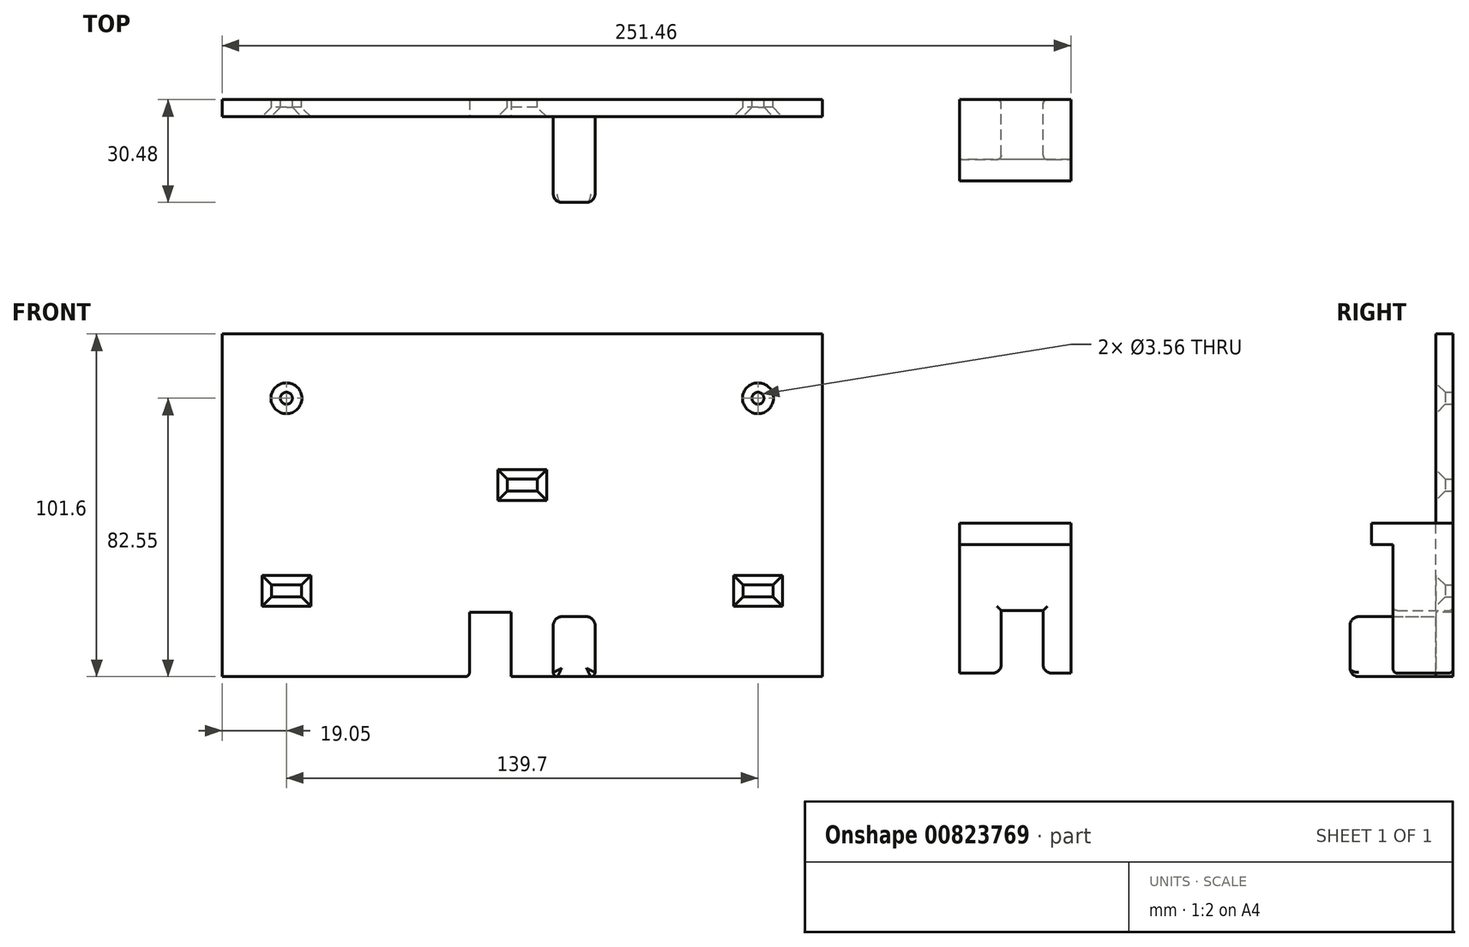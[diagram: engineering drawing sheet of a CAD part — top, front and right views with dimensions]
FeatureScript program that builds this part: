
annotation { "Feature Type Name" : "Feature", "Feature Type Description" : "" }
export const myFeature = defineFeature(function(context is Context, id is Id, definition is map)
    precondition{}
    {
        {
            var Q0;
            Q0=qCreatedBy(makeId("Front.planeOp"),FACE);
            var sketch = newSketch(context, id + "F0", { "sketchPlane" : qUnion([Q0])});
            skLineSegment(sketch, "E0.bottom", {"start": v(27.94, 8.9) * mm, "end": v(-27.94, 8.9) * mm});
            skLineSegment(sketch, "E0.top", {"start": v(27.94, -8.9) * mm, "end": v(-27.94, -8.9) * mm});
            skLineSegment(sketch, "E0.left", {"start": v(27.94, 8.9) * mm, "end": v(27.94, -8.9) * mm});
            skLineSegment(sketch, "E0.right", {"start": v(-27.94, 8.9) * mm, "end": v(-27.94, -8.9) * mm});
            skPoint(sketch, "E0.middle", {"position": v(0, 0) * mm});
            skSolve(sketch);
        }
        {
            var Q0;
            Q0=makeQuery(id+"F0.imprint","IMPRINT",FACE,{"disambiguationData":[TD([[makeQuery(id+"F0.imprint","IMPRINT",EDGE,{"derivedFrom":sQuery(id+"F0.wireOp",EDGE,"E0.bottom")}),1.0]])]});
            extrude(context, id + "F1", {"entities" : qUnion([Q0]), "depth" : 5.08 * mm, "offsetDistance" : 25.4 * mm});
        }
        {
            var Q0;
            Q0=makeQuery(id+"F1.opExtrude","CAP_FACE",FACE,{"disambiguationData":[OSD([sQuery(id+"F0.wireOp",EDGE,"E0.bottom"),sQuery(id+"F0.wireOp",EDGE,"E0.top"),sQuery(id+"F0.wireOp",EDGE,"E0.left"),sQuery(id+"F0.wireOp",EDGE,"E0.right")])],"isStart":false});
            var sketch = newSketch(context, id + "F2", { "sketchPlane" : qUnion([Q0])});
            skLineSegment(sketch, "E1.bottom", {"start": v(-15.6, 8.9) * mm, "end": v(-3.2, 8.9) * mm});
            skLineSegment(sketch, "E1.top", {"start": v(-15.6, -8.9) * mm, "end": v(-3.2, -8.9) * mm});
            skLineSegment(sketch, "E1.left", {"start": v(-15.6, 8.9) * mm, "end": v(-15.6, -8.9) * mm});
            skLineSegment(sketch, "E1.right", {"start": v(-3.2, 8.9) * mm, "end": v(-3.2, -8.9) * mm});
            skLineSegment(sketch, "E2.bottom", {"start": v(21.59, 8.9) * mm, "end": v(9.2, 8.9) * mm});
            skLineSegment(sketch, "E2.top", {"start": v(21.6, -8.9) * mm, "end": v(9.2, -8.9) * mm});
            skLineSegment(sketch, "E2.left", {"start": v(21.59, 8.9) * mm, "end": v(21.6, -8.9) * mm});
            skLineSegment(sketch, "E2.right", {"start": v(9.2, 8.9) * mm, "end": v(9.2, -8.9) * mm});
            skSolve(sketch);
        }
        {
            var Q0;
            Q0=makeQuery(id+"F2.imprint","IMPRINT",FACE,{"disambiguationData":[TD([[makeQuery(id+"F2.imprint","IMPRINT",EDGE,{"derivedFrom":sQuery(id+"F2.wireOp",EDGE,"E2.bottom")}),1.0]])]});
            extrude(context, id + "F3", {"entities" : qUnion([Q0]), "operationType" : NewBodyOperationType.ADD, "depth" : 25.4 * mm, "offsetDistance" : 25.4 * mm});
        }
        {
            var Q0;
            Q0=makeQuery(id+"F2.imprint","IMPRINT",FACE,{"disambiguationData":[TD([[makeQuery(id+"F2.imprint","IMPRINT",EDGE,{"derivedFrom":sQuery(id+"F2.wireOp",EDGE,"E1.bottom")}),1.0]])]});
            extrude(context, id + "F4", {"entities" : qUnion([Q0]), "operationType" : NewBodyOperationType.REMOVE, "endBound" : BoundingType.UP_TO_NEXT, "oppositeDirection" : true, "depth" : 25.4 * mm, "offsetDistance" : 25.4 * mm});
        }
        {
            var Q0;
            {var subQ2=sQuery(id+"F2.wireOp",EDGE,"E2.bottom");var subQ3=sQuery(id+"F0.wireOp",EDGE,"E0.left");var subQ6=sQuery(id+"F0.wireOp",EDGE,"E0.bottom");Q0=makeQuery(id+"F4.boolean.opBoolean","SPLIT",FACE,{"disambiguationData":[TD([makeQuery(id+"F1.opExtrude","SWEPT_FACE",FACE,{"disambiguationData":[OSD([subQ3])]})])],"derivedFrom":makeQuery(id+"F3.boolean.opBoolean","MERGE",FACE,{"derivedFrom":[makeQuery(id+"F1.opExtrude","SWEPT_FACE",FACE,{"disambiguationData":[OSD([subQ6])]}),makeQuery(id+"F3.opExtrude","SWEPT_FACE",FACE,{"disambiguationData":[OSD([subQ2])]})]})});}
            var sketch = newSketch(context, id + "F5", { "sketchPlane" : qUnion([Q0])});
            skLineSegment(sketch, "E3.bottom", {"start": v(27.94, 0) * mm, "end": v(-27.94, 0) * mm});
            skLineSegment(sketch, "E3.top", {"start": v(27.94, -5.08) * mm, "end": v(-27.94, -5.08) * mm});
            skLineSegment(sketch, "E3.left", {"start": v(27.94, 0) * mm, "end": v(27.94, -5.08) * mm});
            skLineSegment(sketch, "E3.right", {"start": v(-27.94, 0) * mm, "end": v(-27.94, -5.08) * mm});
            skSolve(sketch);
        }
        {
            var Q0;
            {var subQ6=sQuery(id+"F5.wireOp",EDGE,"E3.left");Q0=makeQuery(id+"F5.imprint","IMPRINT",FACE,{"disambiguationData":[TD([[makeQuery(id+"F5.imprint","IMPRINT",EDGE,{"derivedFrom":subQ6}),1.0]])]});}
            var Q1;
            {var subQ2=sQuery(id+"F5.wireOp",EDGE,"E3.right");Q1=makeQuery(id+"F5.imprint","IMPRINT",FACE,{"disambiguationData":[TD([[makeQuery(id+"F5.imprint","IMPRINT",EDGE,{"derivedFrom":subQ2}),1.0]])]});}
            extrude(context, id + "F6", {"entities" : qUnion([Q0, Q1]), "operationType" : NewBodyOperationType.ADD, "depth" : 6.35 * mm, "offsetDistance" : 25.4 * mm});
        }
        {
            var Q0;
            Q0=makeQuery(id+"F3.opExtrude","SWEPT_EDGE",EDGE,{"disambiguationData":[OSD([sQuery(id+"F0.wireOp",EDGE,"E0.bottom"),sQuery(id+"F2.wireOp",EDGE,"E2.bottom"),sQuery(id+"F2.wireOp",EDGE,"E2.left")])]});
            var Q1;
            Q1=makeQuery(id+"F3.opExtrude","CAP_EDGE",EDGE,{"disambiguationData":[OSD([sQuery(id+"F2.wireOp",EDGE,"E2.bottom")])],"isStart":false});
            var Q2;
            Q2=makeQuery(id+"F3.opExtrude","SWEPT_EDGE",EDGE,{"disambiguationData":[OSD([sQuery(id+"F0.wireOp",EDGE,"E0.bottom"),sQuery(id+"F2.wireOp",EDGE,"E2.bottom"),sQuery(id+"F2.wireOp",EDGE,"E2.right")])]});
            var Q3;
            Q3=makeQuery(id+"F3.opExtrude","CAP_EDGE",EDGE,{"disambiguationData":[OSD([sQuery(id+"F2.wireOp",EDGE,"E2.right")])],"isStart":false});
            var Q4;
            Q4=makeQuery(id+"F3.opExtrude","CAP_EDGE",EDGE,{"disambiguationData":[OSD([sQuery(id+"F2.wireOp",EDGE,"E2.left")])],"isStart":false});
            var Q5;
            Q5=makeQuery(id+"F3.opExtrude","CAP_EDGE",EDGE,{"disambiguationData":[OSD([sQuery(id+"F2.wireOp",EDGE,"E2.top")])],"isStart":false});
            fillet(context, id + "F7", {"entities" : qUnion([Q0, Q1, Q2, Q3, Q4, Q5]), "radius" : 2.54 * mm, "tangentPropagation" : true, "allowEdgeOverflow" : false});
        }
        {
            var Q0;
            Q0=qCreatedBy(makeId("Front.planeOp"),FACE);
            var sketch = newSketch(context, id + "F8", { "sketchPlane" : qUnion([Q0])});
            skLineSegment(sketch, "E4.bottom", {"start": v(129.54, 36.6) * mm, "end": v(162.56, 36.6) * mm});
            skLineSegment(sketch, "E4.top", {"start": v(129.54, -7.84) * mm, "end": v(162.56, -7.84) * mm});
            skLineSegment(sketch, "E4.left", {"start": v(129.54, 36.6) * mm, "end": v(129.54, -7.84) * mm});
            skLineSegment(sketch, "E4.right", {"start": v(162.56, 36.6) * mm, "end": v(162.56, -7.84) * mm});
            skLineSegment(sketch, "E5.bottom", {"start": v(154.33, -7.84) * mm, "end": v(141.94, -7.84) * mm});
            skLineSegment(sketch, "E5.top", {"start": v(154.33, 10.7) * mm, "end": v(141.94, 10.7) * mm});
            skLineSegment(sketch, "E5.left", {"start": v(154.33, -7.84) * mm, "end": v(154.33, 10.7) * mm});
            skLineSegment(sketch, "E5.right", {"start": v(141.94, -7.84) * mm, "end": v(141.94, 10.7) * mm});
            skSolve(sketch);
        }
        {
            var Q0;
            Q0=makeQuery(id+"F8.imprint","IMPRINT",FACE,{"disambiguationData":[TD([[makeQuery(id+"F8.imprint","IMPRINT",EDGE,{"derivedFrom":sQuery(id+"F8.wireOp",EDGE,"E4.bottom")}),-1.0]])]});
            extrude(context, id + "F9", {"entities" : qUnion([Q0]), "depth" : 17.78 * mm, "offsetDistance" : 25.4 * mm});
        }
        {
            var Q0;
            Q0=makeQuery(id+"F9.opExtrude","SWEPT_EDGE",EDGE,{"disambiguationData":[OSD([sQuery(id+"F8.wireOp",EDGE,"E4.top"),sQuery(id+"F8.wireOp",EDGE,"E5.bottom"),sQuery(id+"F8.wireOp",EDGE,"E5.right")])]});
            var Q1;
            Q1=makeQuery(id+"F9.opExtrude","SWEPT_EDGE",EDGE,{"disambiguationData":[OSD([sQuery(id+"F8.wireOp",EDGE,"E4.top"),sQuery(id+"F8.wireOp",EDGE,"E5.bottom"),sQuery(id+"F8.wireOp",EDGE,"E5.left")])]});
            fillet(context, id + "F10", {"entities" : qUnion([Q0, Q1]), "radius" : 2.54 * mm, "tangentPropagation" : true, "allowEdgeOverflow" : false});
        }
        {
            var Q0;
            Q0=makeQuery(id+"F9.opExtrude","CAP_FACE",FACE,{"disambiguationData":[OSD([sQuery(id+"F8.wireOp",EDGE,"E4.bottom"),sQuery(id+"F8.wireOp",EDGE,"E4.top"),sQuery(id+"F8.wireOp",EDGE,"E4.left"),sQuery(id+"F8.wireOp",EDGE,"E4.right"),sQuery(id+"F8.wireOp",EDGE,"E5.top"),sQuery(id+"F8.wireOp",EDGE,"E5.left"),sQuery(id+"F8.wireOp",EDGE,"E5.right")])],"isStart":false});
            var sketch = newSketch(context, id + "F11", { "sketchPlane" : qUnion([Q0])});
            skLineSegment(sketch, "E6.bottom", {"start": v(162.56, 36.6) * mm, "end": v(129.54, 36.6) * mm});
            skLineSegment(sketch, "E6.top", {"start": v(162.56, 30.26) * mm, "end": v(129.54, 30.26) * mm});
            skLineSegment(sketch, "E6.left", {"start": v(162.56, 36.6) * mm, "end": v(162.56, 30.26) * mm});
            skLineSegment(sketch, "E6.right", {"start": v(129.54, 36.6) * mm, "end": v(129.54, 30.26) * mm});
            skSolve(sketch);
        }
        {
            var Q0;
            Q0=makeQuery(id+"F11.imprint","IMPRINT",FACE,{"disambiguationData":[TD([[makeQuery(id+"F11.imprint","IMPRINT",EDGE,{"derivedFrom":sQuery(id+"F11.wireOp",EDGE,"E6.bottom")}),-1.0]])]});
            extrude(context, id + "F12", {"entities" : qUnion([Q0]), "operationType" : NewBodyOperationType.ADD, "depth" : 6.35 * mm, "offsetDistance" : 25.4 * mm});
        }
        {
            var Q0;
            Q0=makeQuery(id+"F4.boolean.opBoolean","COPY",EDGE,{"derivedFrom":makeQuery(id+"F4.opExtrude","SWEPT_EDGE",EDGE,{"disambiguationData":[OSD([sQuery(id+"F0.wireOp",EDGE,"E0.top"),sQuery(id+"F2.wireOp",EDGE,"E1.top"),sQuery(id+"F2.wireOp",EDGE,"E1.left")])]})});
            var Q1;
            Q1=makeQuery(id+"F4.boolean.opBoolean","COPY",EDGE,{"derivedFrom":makeQuery(id+"F4.opExtrude","SWEPT_EDGE",EDGE,{"disambiguationData":[OSD([sQuery(id+"F0.wireOp",EDGE,"E0.top"),sQuery(id+"F2.wireOp",EDGE,"E1.top"),sQuery(id+"F2.wireOp",EDGE,"E1.right")])]})});
            var Q2;
            Q2=makeQuery(id+"F3.opExtrude","SWEPT_EDGE",EDGE,{"disambiguationData":[OSD([sQuery(id+"F0.wireOp",EDGE,"E0.top"),sQuery(id+"F2.wireOp",EDGE,"E2.top"),sQuery(id+"F2.wireOp",EDGE,"E2.right")])]});
            var Q3;
            Q3=makeQuery(id+"F3.opExtrude","SWEPT_EDGE",EDGE,{"disambiguationData":[OSD([sQuery(id+"F0.wireOp",EDGE,"E0.top"),sQuery(id+"F2.wireOp",EDGE,"E2.top"),sQuery(id+"F2.wireOp",EDGE,"E2.left")])]});
            var Q4;
            Q4=makeQuery(id+"F9.opExtrude","CAP_EDGE",EDGE,{"disambiguationData":[OSD([sQuery(id+"F8.wireOp",EDGE,"E5.right")])],"isStart":true});
            var Q5;
            Q5=makeQuery(id+"F9.opExtrude","CAP_EDGE",EDGE,{"disambiguationData":[OSD([sQuery(id+"F8.wireOp",EDGE,"E5.top")])],"isStart":true});
            var Q6;
            Q6=makeQuery(id+"F9.opExtrude","CAP_EDGE",EDGE,{"disambiguationData":[OSD([sQuery(id+"F8.wireOp",EDGE,"E5.left")])],"isStart":true});
            var Q7;
            Q7=makeQuery(id+"F9.opExtrude","CAP_EDGE",EDGE,{"disambiguationData":[OSD([sQuery(id+"F8.wireOp",EDGE,"E5.left")])],"isStart":false});
            var Q8;
            Q8=makeQuery(id+"F9.opExtrude","CAP_EDGE",EDGE,{"disambiguationData":[OSD([sQuery(id+"F8.wireOp",EDGE,"E5.top")])],"isStart":false});
            var Q9;
            Q9=makeQuery(id+"F9.opExtrude","CAP_EDGE",EDGE,{"disambiguationData":[OSD([sQuery(id+"F8.wireOp",EDGE,"E5.right")])],"isStart":false});
            fillet(context, id + "F13", {"entities" : qUnion([Q0, Q1, Q2, Q3, Q4, Q5, Q6, Q7, Q8, Q9]), "radius" : 1.27 * mm, "tangentPropagation" : true, "allowEdgeOverflow" : false});
        }
        {
            var Q0;
            {var subQ2=sQuery(id+"F0.wireOp",EDGE,"E0.top");var subQ4=sQuery(id+"F0.wireOp",EDGE,"E0.bottom");var subQ6=makeQuery(id+"F3.opExtrude","SWEPT_FACE",FACE,{"disambiguationData":[OSD([sQuery(id+"F2.wireOp",EDGE,"E2.right")])]});var subQ7=sQuery(id+"F0.wireOp",EDGE,"E0.right");var subQ8=makeQuery(id+"F1.opExtrude","SWEPT_FACE",FACE,{"disambiguationData":[OSD([subQ7])]});var subQ9=sQuery(id+"F0.wireOp",EDGE,"E0.left");var subQ10=makeQuery(id+"F1.opExtrude","CAP_FACE",FACE,{"disambiguationData":[OSD([subQ4,subQ2,subQ9,subQ7])],"isStart":false});var subQ11=makeQuery(id+"F3.boolean.opBoolean","SPLIT",FACE,{"disambiguationData":[TD([subQ8])],"derivedFrom":subQ10});Q0=makeQuery(id+"F6.boolean.opBoolean","MERGE",FACE,{"derivedFrom":[makeQuery(id+"F3.boolean.opBoolean","SPLIT",FACE,{"disambiguationData":[TD([makeQuery(id+"F1.opExtrude","SWEPT_FACE",FACE,{"disambiguationData":[OSD([subQ9])]})])],"derivedFrom":subQ10}),makeQuery(id+"F4.boolean.opBoolean","SPLIT",FACE,{"disambiguationData":[TD([subQ8])],"derivedFrom":subQ11}),makeQuery(id+"F4.boolean.opBoolean","SPLIT",FACE,{"disambiguationData":[TD([subQ6])],"derivedFrom":subQ11}),makeQuery(id+"F6.opExtrude","SWEPT_FACE",FACE,{"disambiguationData":[OSD([sQuery(id+"F5.wireOp",EDGE,"E3.top")])]})]});}
            var sketch = newSketch(context, id + "F14", { "sketchPlane" : qUnion([Q0])});
            skLineSegment(sketch, "E7.bottom", {"start": v(-15.6, 8.9) * mm, "end": v(-3.2, 8.9) * mm});
            skLineSegment(sketch, "E7.top", {"start": v(-15.6, 10.16) * mm, "end": v(-3.2, 10.16) * mm});
            skLineSegment(sketch, "E7.left", {"start": v(-15.6, 8.9) * mm, "end": v(-15.6, 10.16) * mm});
            skLineSegment(sketch, "E7.right", {"start": v(-3.2, 8.9) * mm, "end": v(-3.2, 10.16) * mm});
            skSolve(sketch);
        }
        {
            var Q0;
            Q0=makeQuery(id+"F14.imprint","IMPRINT",FACE,{"disambiguationData":[TD([[makeQuery(id+"F14.imprint","IMPRINT",EDGE,{"derivedFrom":sQuery(id+"F14.wireOp",EDGE,"E7.bottom")}),-1.0]])]});
            extrude(context, id + "F15", {"entities" : qUnion([Q0]), "operationType" : NewBodyOperationType.REMOVE, "endBound" : BoundingType.UP_TO_NEXT, "oppositeDirection" : true, "depth" : 25.4 * mm, "offsetDistance" : 25.4 * mm});
        }
        {
            var Q0;
            {var subQ1=sQuery(id+"F0.wireOp",EDGE,"E0.top");var subQ3=sQuery(id+"F0.wireOp",EDGE,"E0.right");var subQ4=sQuery(id+"F0.wireOp",EDGE,"E0.bottom");var subQ7=sQuery(id+"F0.wireOp",EDGE,"E0.left");var subQ8=makeQuery(id+"F1.opExtrude","CAP_FACE",FACE,{"disambiguationData":[OSD([subQ4,subQ1,subQ7,subQ3])],"isStart":true});Q0=makeQuery(id+"F6.boolean.opBoolean","MERGE",FACE,{"derivedFrom":[makeQuery(id+"F4.boolean.opBoolean","SPLIT",FACE,{"disambiguationData":[TD([makeQuery(id+"F1.opExtrude","SWEPT_FACE",FACE,{"disambiguationData":[OSD([subQ7])]})])],"derivedFrom":subQ8}),makeQuery(id+"F4.boolean.opBoolean","SPLIT",FACE,{"disambiguationData":[TD([makeQuery(id+"F1.opExtrude","SWEPT_FACE",FACE,{"disambiguationData":[OSD([subQ3])]})])],"derivedFrom":subQ8}),makeQuery(id+"F6.opExtrude","SWEPT_FACE",FACE,{"disambiguationData":[OSD([sQuery(id+"F5.wireOp",EDGE,"E3.bottom")])]})]});}
            var sketch = newSketch(context, id + "F16", { "sketchPlane" : qUnion([Q0])});
            skLineSegment(sketch, "E8.bottom", {"start": v(-88.9, -8.9) * mm, "end": v(88.9, -8.9) * mm});
            skLineSegment(sketch, "E8.top", {"start": v(-88.9, 92.71) * mm, "end": v(88.9, 92.71) * mm});
            skLineSegment(sketch, "E8.left", {"start": v(-88.9, -8.9) * mm, "end": v(-88.9, 92.71) * mm});
            skLineSegment(sketch, "E8.right", {"start": v(88.9, -8.9) * mm, "end": v(88.9, 92.71) * mm});
            skPoint(sketch, "E9", {"position": v(0, 92.71) * mm});
            skCircle(sketch, "E10", {"center": v(0, 47.9) * mm, "radius": 1.78 * mm});
            skCircle(sketch, "E11", {"center": v(69.85, 73.66) * mm, "radius": 1.78 * mm});
            skCircle(sketch, "E12", {"center": v(69.85, 16.51) * mm, "radius": 1.78 * mm});
            skCircle(sketch, "E13", {"center": v(-69.85, 73.66) * mm, "radius": 1.78 * mm});
            skCircle(sketch, "E14", {"center": v(-69.85, 16.51) * mm, "radius": 1.78 * mm});
            skLineSegment(sketch, "E15.bottom", {"start": v(65.4, 18.29) * mm, "end": v(74.3, 18.29) * mm});
            skLineSegment(sketch, "E15.top", {"start": v(65.4, 14.73) * mm, "end": v(74.3, 14.73) * mm});
            skLineSegment(sketch, "E15.left", {"start": v(65.4, 18.29) * mm, "end": v(65.4, 14.73) * mm});
            skLineSegment(sketch, "E15.right", {"start": v(74.3, 18.29) * mm, "end": v(74.3, 14.73) * mm});
            skLineSegment(sketch, "E16.MirrorCS", {"start": v(-65.4, 14.73) * mm, "end": v(-74.3, 14.73) * mm});
            skLineSegment(sketch, "E17.MirrorCS", {"start": v(-65.4, 18.29) * mm, "end": v(-65.4, 14.73) * mm});
            skLineSegment(sketch, "E18.MirrorCS", {"start": v(-65.4, 18.29) * mm, "end": v(-74.3, 18.29) * mm});
            skLineSegment(sketch, "E19.MirrorCS", {"start": v(-74.3, 18.29) * mm, "end": v(-74.3, 14.73) * mm});
            skLineSegment(sketch, "E20.bottom", {"start": v(-4.45, 49.68) * mm, "end": v(4.45, 49.68) * mm});
            skLineSegment(sketch, "E20.top", {"start": v(-4.45, 46.13) * mm, "end": v(4.45, 46.13) * mm});
            skLineSegment(sketch, "E20.left", {"start": v(-4.45, 49.68) * mm, "end": v(-4.45, 46.13) * mm});
            skLineSegment(sketch, "E20.right", {"start": v(4.45, 49.68) * mm, "end": v(4.45, 46.13) * mm});
            skSolve(sketch);
        }
        {
            var Q0;
            Q0=makeQuery(id+"F16.imprint","IMPRINT",FACE,{"disambiguationData":[TD([[makeQuery(id+"F16.imprint","IMPRINT",EDGE,{"derivedFrom":sQuery(id+"F16.wireOp",EDGE,"E8.top")}),-1.0]])]});
            var Q1;
            {var subQ2=sQuery(id+"F0.wireOp",EDGE,"E0.top");var subQ4=sQuery(id+"F0.wireOp",EDGE,"E0.bottom");var subQ6=makeQuery(id+"F3.opExtrude","SWEPT_FACE",FACE,{"disambiguationData":[OSD([sQuery(id+"F2.wireOp",EDGE,"E2.right")])]});var subQ7=sQuery(id+"F0.wireOp",EDGE,"E0.right");var subQ8=makeQuery(id+"F1.opExtrude","SWEPT_FACE",FACE,{"disambiguationData":[OSD([subQ7])]});var subQ9=sQuery(id+"F0.wireOp",EDGE,"E0.left");var subQ10=makeQuery(id+"F1.opExtrude","CAP_FACE",FACE,{"disambiguationData":[OSD([subQ4,subQ2,subQ9,subQ7])],"isStart":false});var subQ11=makeQuery(id+"F3.boolean.opBoolean","SPLIT",FACE,{"disambiguationData":[TD([subQ8])],"derivedFrom":subQ10});Q1=makeQuery(id+"F6.boolean.opBoolean","MERGE",FACE,{"derivedFrom":[makeQuery(id+"F3.boolean.opBoolean","SPLIT",FACE,{"disambiguationData":[TD([makeQuery(id+"F1.opExtrude","SWEPT_FACE",FACE,{"disambiguationData":[OSD([subQ9])]})])],"derivedFrom":subQ10}),makeQuery(id+"F4.boolean.opBoolean","SPLIT",FACE,{"disambiguationData":[TD([subQ8])],"derivedFrom":subQ11}),makeQuery(id+"F4.boolean.opBoolean","SPLIT",FACE,{"disambiguationData":[TD([subQ6])],"derivedFrom":subQ11}),makeQuery(id+"F6.opExtrude","SWEPT_FACE",FACE,{"disambiguationData":[OSD([sQuery(id+"F5.wireOp",EDGE,"E3.top")])]})]});}
            extrude(context, id + "F17", {"entities" : qUnion([Q0]), "operationType" : NewBodyOperationType.ADD, "endBound" : BoundingType.UP_TO_SURFACE, "oppositeDirection" : true, "depth" : 25.4 * mm, "endBoundEntityFace" : qUnion([Q1]), "offsetDistance" : 25.4 * mm});
        }
        {
            var Q0;
            Q0=makeQuery(id+"F17.opExtrude","CAP_EDGE",EDGE,{"disambiguationData":[OSD([sQuery(id+"F16.wireOp",EDGE,"E11")])],"isStart":false});
            var Q1;
            {var subQ2=sQuery(id+"F0.wireOp",EDGE,"E0.top");var subQ4=sQuery(id+"F0.wireOp",EDGE,"E0.bottom");var subQ6=makeQuery(id+"F3.opExtrude","SWEPT_FACE",FACE,{"disambiguationData":[OSD([sQuery(id+"F2.wireOp",EDGE,"E2.right")])]});var subQ7=sQuery(id+"F0.wireOp",EDGE,"E0.right");var subQ8=makeQuery(id+"F1.opExtrude","SWEPT_FACE",FACE,{"disambiguationData":[OSD([subQ7])]});var subQ9=sQuery(id+"F0.wireOp",EDGE,"E0.left");var subQ10=makeQuery(id+"F1.opExtrude","CAP_FACE",FACE,{"disambiguationData":[OSD([subQ4,subQ2,subQ9,subQ7])],"isStart":false});var subQ11=makeQuery(id+"F3.boolean.opBoolean","SPLIT",FACE,{"disambiguationData":[TD([subQ8])],"derivedFrom":subQ10});Q1=makeQuery(id+"F17.opExtrude","TWEAK_EDGE",EDGE,{"derivedFrom":[makeQuery(id+"F6.boolean.opBoolean","MERGE",FACE,{"derivedFrom":[makeQuery(id+"F3.boolean.opBoolean","SPLIT",FACE,{"disambiguationData":[TD([makeQuery(id+"F1.opExtrude","SWEPT_FACE",FACE,{"disambiguationData":[OSD([subQ9])]})])],"derivedFrom":subQ10}),makeQuery(id+"F4.boolean.opBoolean","SPLIT",FACE,{"disambiguationData":[TD([subQ8])],"derivedFrom":subQ11}),makeQuery(id+"F4.boolean.opBoolean","SPLIT",FACE,{"disambiguationData":[TD([subQ6])],"derivedFrom":subQ11}),makeQuery(id+"F6.opExtrude","SWEPT_FACE",FACE,{"disambiguationData":[OSD([sQuery(id+"F5.wireOp",EDGE,"E3.top")])]})]}),makeQuery(id+"F16.imprint","IMPRINT",EDGE,{"derivedFrom":sQuery(id+"F16.wireOp",EDGE,"E10")})]});}
            var Q2;
            Q2=makeQuery(id+"F17.opExtrude","CAP_EDGE",EDGE,{"disambiguationData":[OSD([sQuery(id+"F16.wireOp",EDGE,"E13")])],"isStart":false});
            var Q3;
            {var subQ2=sQuery(id+"F0.wireOp",EDGE,"E0.top");var subQ4=sQuery(id+"F0.wireOp",EDGE,"E0.bottom");var subQ6=makeQuery(id+"F3.opExtrude","SWEPT_FACE",FACE,{"disambiguationData":[OSD([sQuery(id+"F2.wireOp",EDGE,"E2.right")])]});var subQ7=sQuery(id+"F0.wireOp",EDGE,"E0.right");var subQ8=makeQuery(id+"F1.opExtrude","SWEPT_FACE",FACE,{"disambiguationData":[OSD([subQ7])]});var subQ9=sQuery(id+"F0.wireOp",EDGE,"E0.left");var subQ10=makeQuery(id+"F1.opExtrude","CAP_FACE",FACE,{"disambiguationData":[OSD([subQ4,subQ2,subQ9,subQ7])],"isStart":false});var subQ11=makeQuery(id+"F3.boolean.opBoolean","SPLIT",FACE,{"disambiguationData":[TD([subQ8])],"derivedFrom":subQ10});Q3=makeQuery(id+"F17.opExtrude","TWEAK_EDGE",EDGE,{"derivedFrom":[makeQuery(id+"F6.boolean.opBoolean","MERGE",FACE,{"derivedFrom":[makeQuery(id+"F3.boolean.opBoolean","SPLIT",FACE,{"disambiguationData":[TD([makeQuery(id+"F1.opExtrude","SWEPT_FACE",FACE,{"disambiguationData":[OSD([subQ9])]})])],"derivedFrom":subQ10}),makeQuery(id+"F4.boolean.opBoolean","SPLIT",FACE,{"disambiguationData":[TD([subQ8])],"derivedFrom":subQ11}),makeQuery(id+"F4.boolean.opBoolean","SPLIT",FACE,{"disambiguationData":[TD([subQ6])],"derivedFrom":subQ11}),makeQuery(id+"F6.opExtrude","SWEPT_FACE",FACE,{"disambiguationData":[OSD([sQuery(id+"F5.wireOp",EDGE,"E3.top")])]})]}),makeQuery(id+"F16.imprint","IMPRINT",EDGE,{"derivedFrom":sQuery(id+"F16.wireOp",EDGE,"E14")})]});}
            var Q4;
            {var subQ2=sQuery(id+"F0.wireOp",EDGE,"E0.top");var subQ4=sQuery(id+"F0.wireOp",EDGE,"E0.bottom");var subQ6=makeQuery(id+"F3.opExtrude","SWEPT_FACE",FACE,{"disambiguationData":[OSD([sQuery(id+"F2.wireOp",EDGE,"E2.right")])]});var subQ7=sQuery(id+"F0.wireOp",EDGE,"E0.right");var subQ8=makeQuery(id+"F1.opExtrude","SWEPT_FACE",FACE,{"disambiguationData":[OSD([subQ7])]});var subQ9=sQuery(id+"F0.wireOp",EDGE,"E0.left");var subQ10=makeQuery(id+"F1.opExtrude","CAP_FACE",FACE,{"disambiguationData":[OSD([subQ4,subQ2,subQ9,subQ7])],"isStart":false});var subQ11=makeQuery(id+"F3.boolean.opBoolean","SPLIT",FACE,{"disambiguationData":[TD([subQ8])],"derivedFrom":subQ10});Q4=makeQuery(id+"F17.opExtrude","TWEAK_EDGE",EDGE,{"derivedFrom":[makeQuery(id+"F6.boolean.opBoolean","MERGE",FACE,{"derivedFrom":[makeQuery(id+"F3.boolean.opBoolean","SPLIT",FACE,{"disambiguationData":[TD([makeQuery(id+"F1.opExtrude","SWEPT_FACE",FACE,{"disambiguationData":[OSD([subQ9])]})])],"derivedFrom":subQ10}),makeQuery(id+"F4.boolean.opBoolean","SPLIT",FACE,{"disambiguationData":[TD([subQ8])],"derivedFrom":subQ11}),makeQuery(id+"F4.boolean.opBoolean","SPLIT",FACE,{"disambiguationData":[TD([subQ6])],"derivedFrom":subQ11}),makeQuery(id+"F6.opExtrude","SWEPT_FACE",FACE,{"disambiguationData":[OSD([sQuery(id+"F5.wireOp",EDGE,"E3.top")])]})]}),makeQuery(id+"F16.imprint","IMPRINT",EDGE,{"derivedFrom":sQuery(id+"F16.wireOp",EDGE,"E12")})]});}
            var Q5;
            Q5=makeQuery(id+"F17.opExtrude","CAP_EDGE",EDGE,{"disambiguationData":[OSD([sQuery(id+"F16.wireOp",EDGE,"E15.top")])],"isStart":false});
            var Q6;
            Q6=makeQuery(id+"F17.opExtrude","CAP_EDGE",EDGE,{"disambiguationData":[OSD([sQuery(id+"F16.wireOp",EDGE,"E15.left")])],"isStart":false});
            var Q7;
            Q7=makeQuery(id+"F17.opExtrude","CAP_EDGE",EDGE,{"disambiguationData":[OSD([sQuery(id+"F16.wireOp",EDGE,"E15.bottom")])],"isStart":false});
            var Q8;
            Q8=makeQuery(id+"F17.opExtrude","CAP_EDGE",EDGE,{"disambiguationData":[OSD([sQuery(id+"F16.wireOp",EDGE,"E15.right")])],"isStart":false});
            var Q9;
            Q9=makeQuery(id+"F17.opExtrude","CAP_EDGE",EDGE,{"disambiguationData":[OSD([sQuery(id+"F16.wireOp",EDGE,"E16.MirrorCS")])],"isStart":false});
            var Q10;
            Q10=makeQuery(id+"F17.opExtrude","CAP_EDGE",EDGE,{"disambiguationData":[OSD([sQuery(id+"F16.wireOp",EDGE,"E18.MirrorCS")])],"isStart":false});
            var Q11;
            Q11=makeQuery(id+"F17.opExtrude","CAP_EDGE",EDGE,{"disambiguationData":[OSD([sQuery(id+"F16.wireOp",EDGE,"E19.MirrorCS")])],"isStart":false});
            var Q12;
            Q12=makeQuery(id+"F17.opExtrude","CAP_EDGE",EDGE,{"disambiguationData":[OSD([sQuery(id+"F16.wireOp",EDGE,"E17.MirrorCS")])],"isStart":false});
            var Q13;
            Q13=makeQuery(id+"F17.opExtrude","CAP_EDGE",EDGE,{"disambiguationData":[OSD([sQuery(id+"F16.wireOp",EDGE,"E20.bottom")])],"isStart":false});
            var Q14;
            Q14=makeQuery(id+"F17.opExtrude","CAP_EDGE",EDGE,{"disambiguationData":[OSD([sQuery(id+"F16.wireOp",EDGE,"E20.right")])],"isStart":false});
            var Q15;
            Q15=makeQuery(id+"F17.opExtrude","CAP_EDGE",EDGE,{"disambiguationData":[OSD([sQuery(id+"F16.wireOp",EDGE,"E20.top")])],"isStart":false});
            var Q16;
            Q16=makeQuery(id+"F17.opExtrude","CAP_EDGE",EDGE,{"disambiguationData":[OSD([sQuery(id+"F16.wireOp",EDGE,"E20.left")])],"isStart":false});
            chamfer(context, id + "F18", {"entities" : qUnion([Q0, Q1, Q2, Q3, Q4, Q5, Q6, Q7, Q8, Q9, Q10, Q11, Q12, Q13, Q14, Q15, Q16]), "width" : 2.8 * mm, "tangentPropagation" : true});
        }
    });
